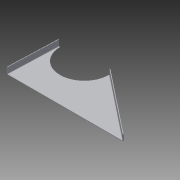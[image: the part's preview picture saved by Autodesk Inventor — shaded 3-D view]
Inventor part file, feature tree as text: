
AUTODESK INVENTOR PART (.ipt)
format: ipt  version: 2013 (Build 170138000, 138)  size: 118,272 bytes
history: native  units: in
note: dims shown in document units (in); Inventor stores cm internally (conversion verified against a paired STEP export)
features: sheet_metal_op x4, sketch x2, other x2
ambient origin geometry x8: Origin, YZ Plane, XZ Plane, XY Plane, X Axis, Y Axis, Z Axis, Center Point
bodies: Solid1 (feature_tree)
feature tree (8):
  sheet_metal_op  "Face1"
  sheet_metal_op  "Flange1"
  sketch  "Sketch1"  dims[d0=11.547in d1=1.4in d2=1.0in d3=27.0in d4=12.0in d5=11.25in]
  other  "Plate1"
  sketch  "Sketch2"  dims[d6=0.12in d7=0.12in d8=0.06in d9=0.24in d10=0.12in d11=1.5in d12=90.0deg d13=0.12in d14=0.48in d15=0.12in d16=0.12in]
  other  "Plate2"
  sheet_metal_op  "Bend1"
  sheet_metal_op  "Corner1"
